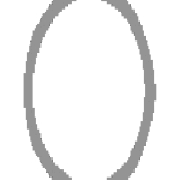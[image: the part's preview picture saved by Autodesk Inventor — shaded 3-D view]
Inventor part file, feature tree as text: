
AUTODESK INVENTOR PART (.ipt)
format: ipt  version: 2021 (Build 250183000, 183)  size: 141,824 bytes
history: native  units: in
note: dims shown in document units (in); Inventor stores cm internally (conversion verified against a paired STEP export)
features: plane x7, sketch x5, other x4, extrude x2, boolean_combine x2
ambient origin geometry x8: Origin, YZ Plane, XZ Plane, XY Plane, X Axis, Y Axis, Z Axis, Center Point
bodies: Solid1 (feature_tree), Body (feature_tree), Solid2 (feature_tree), Solid3 (feature_tree)
feature tree (20):
  other  "Driven Length"
  other  "Frame Generator"
  other  "Start Plane"
  other  "End Plane"
  plane  "Work Plane4"
  plane  "Work Plane5"
  plane  "Work Plane6"
  extrude  "Extrusion3"  Depth=0.065in
  boolean_combine  "Combine1"
  plane  "Work Plane7"
  plane  "Work Plane8"
  plane  "Work Plane9"
  extrude  "Extrusion4"  TaperAngle=0.0deg  [1 undecoded]
  boolean_combine  "Combine2"
  sketch  "Sketch"  dims[d8=90.0deg d9=5.831in d10=0.12in d11=0.0in d12=0.12in d13=0.0in]
  sketch  "Sketch2"  dims[d0=1.0in d1=0.065in]
  plane  "Work Plane3"
  sketch  "Sketch3"  dims[d2=5.831in d4=-0.0in]
  sketch  "Sketch4"  dims[d5=5.831in]
  sketch  "Sketch5"  dims[d6=0.12in d7=0.0in]
note: 1 required parameter value undecoded (feature->parameter linkage not recoverable at this tier; creation-order binding heuristic only, values carry confidence <= 0.55)
